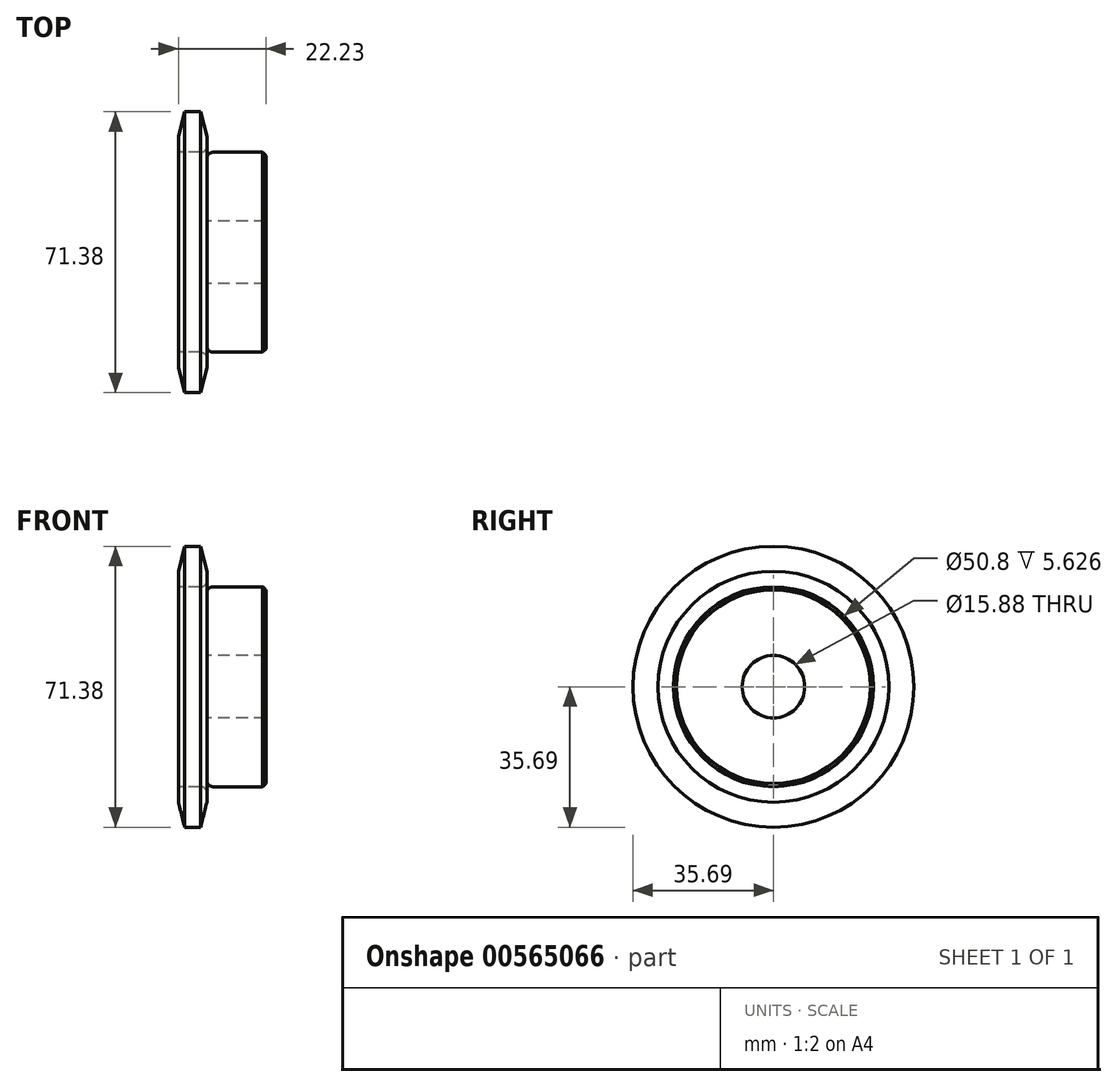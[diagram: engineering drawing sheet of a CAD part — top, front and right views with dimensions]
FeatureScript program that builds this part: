
annotation { "Feature Type Name" : "Feature", "Feature Type Description" : "" }
export const myFeature = defineFeature(function(context is Context, id is Id, definition is map)
    precondition{}
    {
        {
            var Q0;
            Q0=qCreatedBy(makeId("Front.planeOp"),FACE);
            var sketch = newSketch(context, id + "F0", { "sketchPlane" : qUnion([Q0])});
            skLineSegment(sketch, "E0", {"start": v(0, 0) * mm, "end": v(34.37, 0) * mm, "construction": true});
            skLineSegment(sketch, "E1.bottom", {"start": v(0, 35.69) * mm, "end": v(7.21, 35.69) * mm});
            skLineSegment(sketch, "E1.top", {"start": v(0, 7.94) * mm, "end": v(7.21, 7.94) * mm});
            skLineSegment(sketch, "E1.left", {"start": v(0, 35.69) * mm, "end": v(0, 7.94) * mm});
            skLineSegment(sketch, "E1.right", {"start": v(7.21, 35.69) * mm, "end": v(7.21, 7.94) * mm});
            skLineSegment(sketch, "E2.bottom", {"start": v(0, 7.94) * mm, "end": v(22.23, 7.94) * mm});
            skLineSegment(sketch, "E2.top", {"start": v(0, 25.4) * mm, "end": v(22.23, 25.4) * mm});
            skLineSegment(sketch, "E2.left", {"start": v(0, 7.94) * mm, "end": v(0, 25.4) * mm});
            skLineSegment(sketch, "E2.right", {"start": v(22.23, 7.94) * mm, "end": v(22.23, 25.4) * mm});
            skLineSegment(sketch, "E3.MirrorCS", {"start": v(0, -7.94) * mm, "end": v(7.21, -7.94) * mm});
            skLineSegment(sketch, "E4.MirrorCS", {"start": v(22.23, -7.94) * mm, "end": v(22.23, -25.4) * mm});
            skLineSegment(sketch, "E5.MirrorCS", {"start": v(0, -7.94) * mm, "end": v(0, -25.4) * mm});
            skLineSegment(sketch, "E6.MirrorCS", {"start": v(0, -35.69) * mm, "end": v(7.21, -35.69) * mm});
            skLineSegment(sketch, "E7.MirrorCS", {"start": v(0, -35.69) * mm, "end": v(0, -7.94) * mm});
            skLineSegment(sketch, "E8.MirrorCS", {"start": v(0, -25.4) * mm, "end": v(22.23, -25.4) * mm});
            skLineSegment(sketch, "E9.MirrorCS", {"start": v(7.21, -35.69) * mm, "end": v(7.21, -7.94) * mm});
            skLineSegment(sketch, "E10.MirrorCS", {"start": v(0, -7.94) * mm, "end": v(22.23, -7.94) * mm});
            skSolve(sketch);
        }
        {
            var Q0;
            {var subQ0=sQuery(id+"F0.wireOp",EDGE,"E1.bottom");Q0=makeQuery(id+"F0.imprint","IMPRINT",FACE,{"disambiguationData":[TD([[makeQuery(id+"F0.imprint","IMPRINT",EDGE,{"derivedFrom":subQ0}),-1.0]])]});}
            var Q1;
            {var subQ5=sQuery(id+"F0.wireOp",EDGE,"E2.left");Q1=makeQuery(id+"F0.imprint","IMPRINT",FACE,{"disambiguationData":[TD([[makeQuery(id+"F0.imprint","IMPRINT",EDGE,{"derivedFrom":subQ5}),-1.0]])]});}
            var Q2;
            {var subQ5=sQuery(id+"F0.wireOp",EDGE,"E2.right");Q2=makeQuery(id+"F0.imprint","IMPRINT",FACE,{"disambiguationData":[TD([[makeQuery(id+"F0.imprint","IMPRINT",EDGE,{"derivedFrom":subQ5}),1.0]])]});}
            var Q3;
            Q3=sQuery(id+"F0.wireOp",EDGE,"E0");
            revolve(context, id + "F1", {"entities" : qUnion([Q0, Q1, Q2]), "axis" : qUnion([Q3]), "revolveType" : RevolveType.FULL});
        }
        {
            var Q0;
            Q0=makeQuery(id+"F1.opRevolve","SWEPT_EDGE",EDGE,{"disambiguationData":[OSD([sQuery(id+"F0.wireOp",EDGE,"E1.right"),sQuery(id+"F0.wireOp",EDGE,"E2.top")])]});
            fillet(context, id + "F2", {"entities" : qUnion([Q0]), "radius" : 1.59 * mm, "tangentPropagation" : true, "allowEdgeOverflow" : false});
        }
        {
            var Q0;
            Q0=makeQuery(id+"F1.opRevolve","SWEPT_EDGE",EDGE,{"disambiguationData":[OSD([sQuery(id+"F0.wireOp",EDGE,"E2.top"),sQuery(id+"F0.wireOp",EDGE,"E2.right")])]});
            chamfer(context, id + "F3", {"entities" : qUnion([Q0]), "width" : 0.8 * mm, "tangentPropagation" : true});
        }
        {
            var Q0;
            Q0=makeQuery(id+"F1.opRevolve","SWEPT_EDGE",EDGE,{"disambiguationData":[OSD([sQuery(id+"F0.wireOp",EDGE,"E1.bottom"),sQuery(id+"F0.wireOp",EDGE,"E1.left")])]});
            var Q1;
            Q1=makeQuery(id+"F1.opRevolve","SWEPT_EDGE",EDGE,{"disambiguationData":[OSD([sQuery(id+"F0.wireOp",EDGE,"E1.bottom"),sQuery(id+"F0.wireOp",EDGE,"E1.right")])]});
            chamfer(context, id + "F4", {"entities" : qUnion([Q0, Q1]), "chamferType" : ChamferType.TWO_OFFSETS, "width1" : 6.35 * mm, "oppositeDirection" : false, "width2" : 1.57 * mm, "tangentPropagation" : true});
        }
    });
